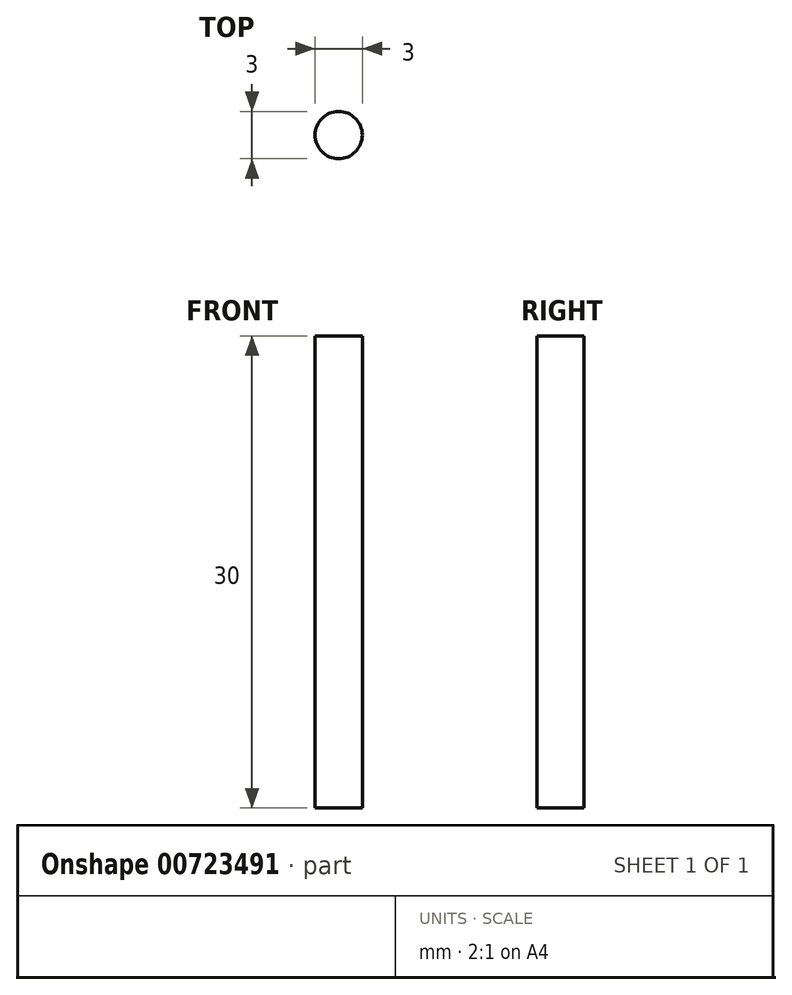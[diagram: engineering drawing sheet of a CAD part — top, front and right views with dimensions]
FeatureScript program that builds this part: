
annotation { "Feature Type Name" : "Feature", "Feature Type Description" : "" }
export const myFeature = defineFeature(function(context is Context, id is Id, definition is map)
    precondition{}
    {
        {
            var Q0;
            Q0=qCreatedBy(makeId("Top.planeOp"),FACE);
            var sketch = newSketch(context, id + "F0", { "sketchPlane" : qUnion([Q0])});
            skCircle(sketch, "E0", {"center": v(0, 0) * mm, "radius": 1.5 * mm});
            skSolve(sketch);
        }
        {
            var Q0;
            Q0 = qSketchRegion(id + "F0", true);
            extrude(context, id + "F1", {"entities" : qUnion([Q0]), "depth" : 30 * mm, "offsetDistance" : 25 * mm});
        }
    });
